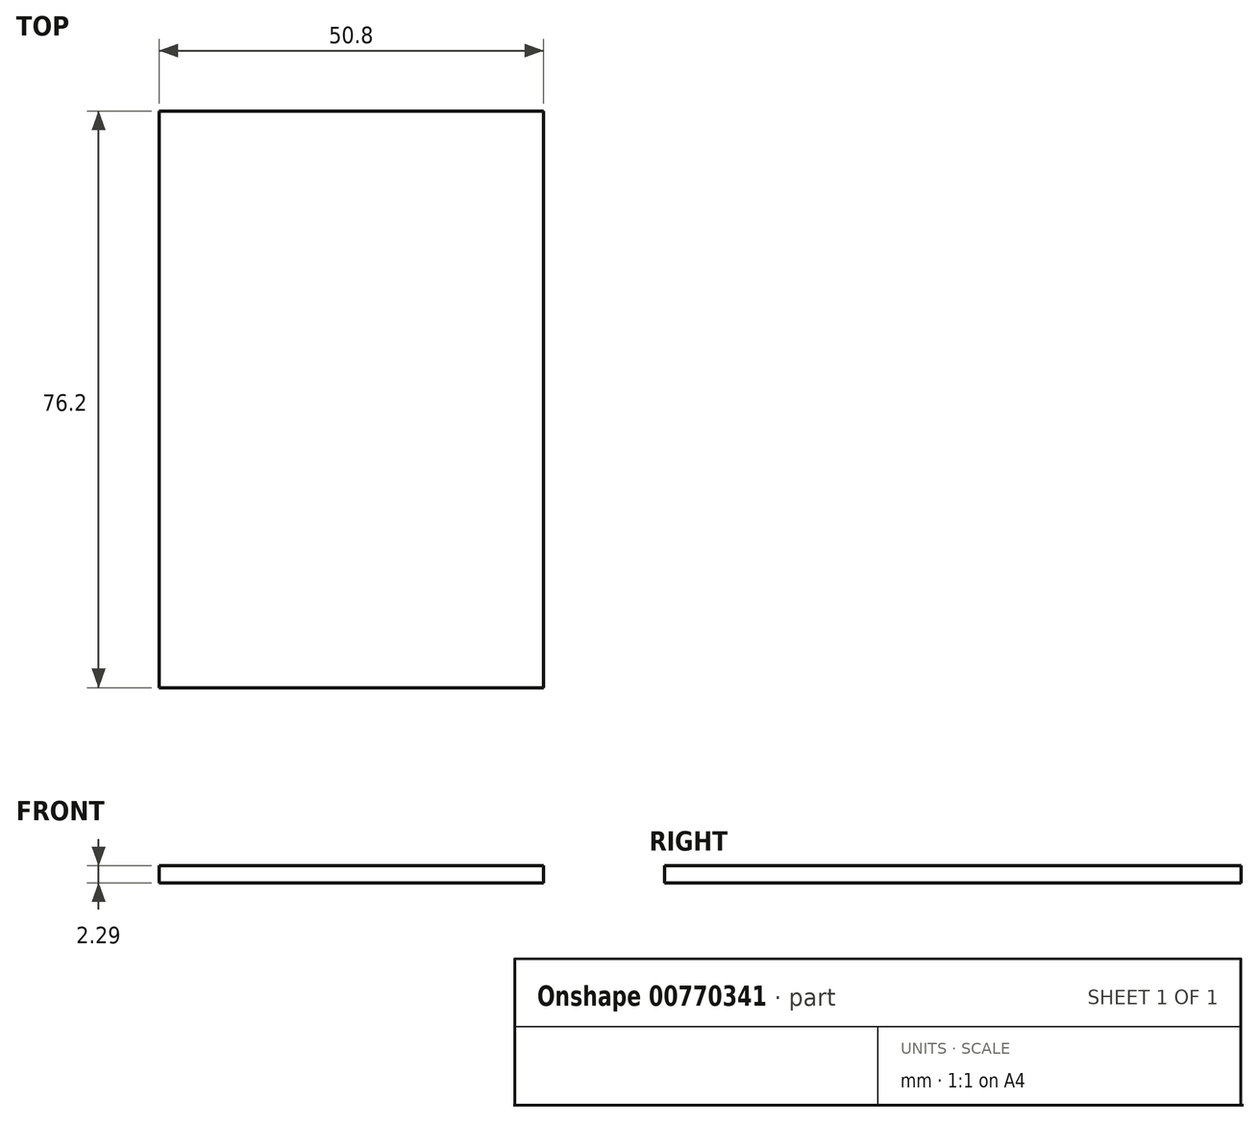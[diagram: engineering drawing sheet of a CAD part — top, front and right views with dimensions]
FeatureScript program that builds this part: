
annotation { "Feature Type Name" : "Feature", "Feature Type Description" : "" }
export const myFeature = defineFeature(function(context is Context, id is Id, definition is map)
    precondition{}
    {
        {
            var Q0;
            Q0=qCreatedBy(makeId("Top.planeOp"),FACE);
            var sketch = newSketch(context, id + "F0", { "sketchPlane" : qUnion([Q0])});
            skLineSegment(sketch, "E0.bottom", {"start": v(0, 0) * mm, "end": v(50.8, 0) * mm});
            skLineSegment(sketch, "E0.top", {"start": v(0, 76.2) * mm, "end": v(50.8, 76.2) * mm});
            skLineSegment(sketch, "E0.left", {"start": v(0, 0) * mm, "end": v(0, 76.2) * mm});
            skLineSegment(sketch, "E0.right", {"start": v(50.8, 0) * mm, "end": v(50.8, 76.2) * mm});
            skSolve(sketch);
        }
        {
            var Q0;
            Q0=makeQuery(id+"F0.imprint","IMPRINT",FACE,{"disambiguationData":[TD([[makeQuery(id+"F0.imprint","IMPRINT",EDGE,{"derivedFrom":sQuery(id+"F0.wireOp",EDGE,"E0.bottom")}),1.0]])]});
            extrude(context, id + "F1", {"entities" : qUnion([Q0]), "depth" : 2.3 * mm, "offsetDistance" : 25.4 * mm});
        }
    });
